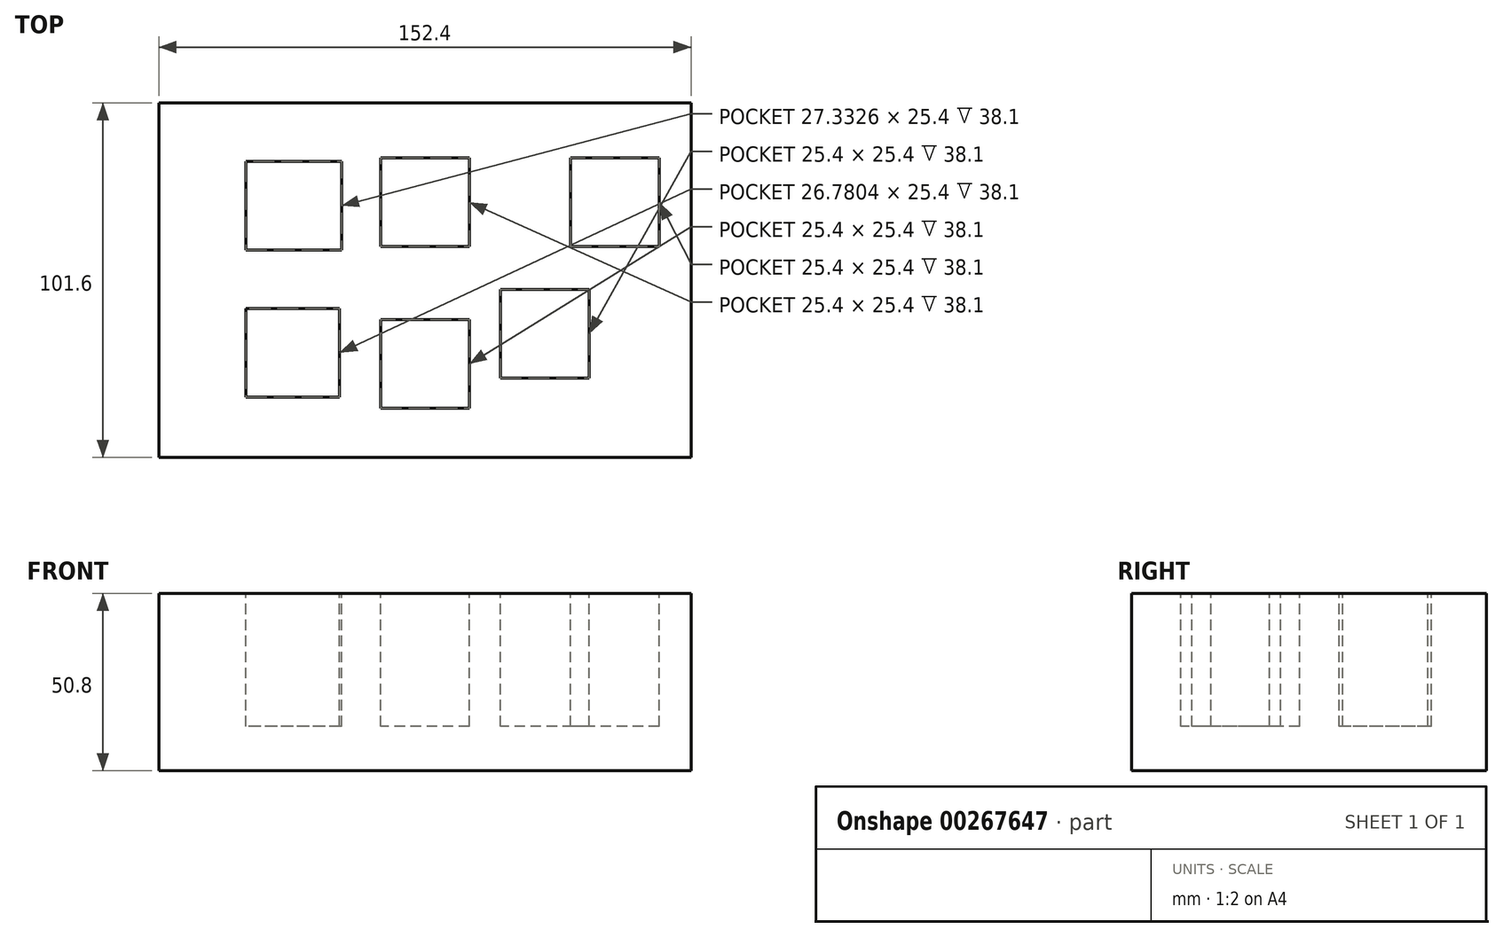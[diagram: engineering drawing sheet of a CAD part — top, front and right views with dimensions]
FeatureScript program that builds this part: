
annotation { "Feature Type Name" : "Feature", "Feature Type Description" : "" }
export const myFeature = defineFeature(function(context is Context, id is Id, definition is map)
    precondition{}
    {
        {
            var Q0;
            Q0=qCreatedBy(makeId("Top.planeOp"),FACE);
            var sketch = newSketch(context, id + "F0", { "sketchPlane" : qUnion([Q0])});
            skLineSegment(sketch, "E0.bottom", {"start": v(76.2, 50.8) * mm, "end": v(-76.2, 50.8) * mm});
            skLineSegment(sketch, "E0.top", {"start": v(76.2, -50.8) * mm, "end": v(-76.2, -50.8) * mm});
            skLineSegment(sketch, "E0.left", {"start": v(76.2, 50.8) * mm, "end": v(76.2, -50.8) * mm});
            skLineSegment(sketch, "E0.right", {"start": v(-76.2, 50.8) * mm, "end": v(-76.2, -50.8) * mm});
            skPoint(sketch, "E0.middle", {"position": v(0, 0) * mm});
            skSolve(sketch);
        }
        {
            var Q0;
            Q0 = qSketchRegion(id + "F0", true);
            extrude(context, id + "F1", {"entities" : qUnion([Q0]), "oppositeDirection" : true, "depth" : 50.8 * mm});
        }
        {
            var Q0;
            Q0=qCreatedBy(makeId("Top.planeOp"),FACE);
            var sketch = newSketch(context, id + "F2", { "sketchPlane" : qUnion([Q0])});
            skLineSegment(sketch, "E1.bottom", {"start": v(-23.88, 34.04) * mm, "end": v(-51.21, 34.04) * mm});
            skLineSegment(sketch, "E1.top", {"start": v(-23.88, 8.64) * mm, "end": v(-51.21, 8.64) * mm});
            skLineSegment(sketch, "E1.left", {"start": v(-23.88, 34.04) * mm, "end": v(-23.88, 8.64) * mm});
            skLineSegment(sketch, "E1.right", {"start": v(-51.21, 34.04) * mm, "end": v(-51.21, 8.64) * mm});
            skPoint(sketch, "E1.middle", {"position": v(-37.55, 21.34) * mm});
            skLineSegment(sketch, "E2.bottom", {"start": v(12.7, 35.06) * mm, "end": v(-12.7, 35.06) * mm});
            skLineSegment(sketch, "E2.top", {"start": v(12.7, 9.66) * mm, "end": v(-12.7, 9.66) * mm});
            skLineSegment(sketch, "E2.left", {"start": v(12.7, 35.06) * mm, "end": v(12.7, 9.66) * mm});
            skLineSegment(sketch, "E2.right", {"start": v(-12.7, 35.06) * mm, "end": v(-12.7, 9.66) * mm});
            skPoint(sketch, "E2.middle", {"position": v(0, 22.36) * mm});
            skLineSegment(sketch, "E3.bottom", {"start": v(67.1, 35.06) * mm, "end": v(41.7, 35.06) * mm});
            skLineSegment(sketch, "E3.top", {"start": v(67.1, 9.66) * mm, "end": v(41.7, 9.66) * mm});
            skLineSegment(sketch, "E3.left", {"start": v(67.1, 35.06) * mm, "end": v(67.1, 9.66) * mm});
            skLineSegment(sketch, "E3.right", {"start": v(41.7, 35.06) * mm, "end": v(41.7, 9.66) * mm});
            skPoint(sketch, "E3.middle", {"position": v(54.4, 22.36) * mm});
            skLineSegment(sketch, "E4.bottom", {"start": v(12.7, -11.3) * mm, "end": v(-12.7, -11.3) * mm});
            skLineSegment(sketch, "E4.top", {"start": v(12.7, -36.7) * mm, "end": v(-12.7, -36.7) * mm});
            skLineSegment(sketch, "E4.left", {"start": v(12.7, -11.3) * mm, "end": v(12.7, -36.7) * mm});
            skLineSegment(sketch, "E4.right", {"start": v(-12.7, -11.3) * mm, "end": v(-12.7, -36.7) * mm});
            skPoint(sketch, "E4.middle", {"position": v(0, -24) * mm});
            skLineSegment(sketch, "E5.bottom", {"start": v(-24.43, -8.13) * mm, "end": v(-51.21, -8.13) * mm});
            skLineSegment(sketch, "E5.top", {"start": v(-24.43, -33.53) * mm, "end": v(-51.21, -33.53) * mm});
            skLineSegment(sketch, "E5.left", {"start": v(-24.43, -8.13) * mm, "end": v(-24.43, -33.53) * mm});
            skLineSegment(sketch, "E5.right", {"start": v(-51.21, -8.13) * mm, "end": v(-51.21, -33.53) * mm});
            skPoint(sketch, "E5.middle", {"position": v(-37.82, -20.83) * mm});
            skLineSegment(sketch, "E6.bottom", {"start": v(47.07, -2.7) * mm, "end": v(21.67, -2.7) * mm});
            skLineSegment(sketch, "E6.top", {"start": v(47.07, -28.1) * mm, "end": v(21.67, -28.1) * mm});
            skLineSegment(sketch, "E6.left", {"start": v(47.07, -2.7) * mm, "end": v(47.07, -28.1) * mm});
            skLineSegment(sketch, "E6.right", {"start": v(21.67, -2.7) * mm, "end": v(21.67, -28.1) * mm});
            skPoint(sketch, "E6.middle", {"position": v(34.37, -15.4) * mm});
            skSolve(sketch);
        }
        {
            var Q0;
            Q0 = qSketchRegion(id + "F2", true);
            extrude(context, id + "F3", {"entities" : qUnion([Q0]), "operationType" : NewBodyOperationType.REMOVE, "oppositeDirection" : true, "depth" : 38.1 * mm});
        }
    });
